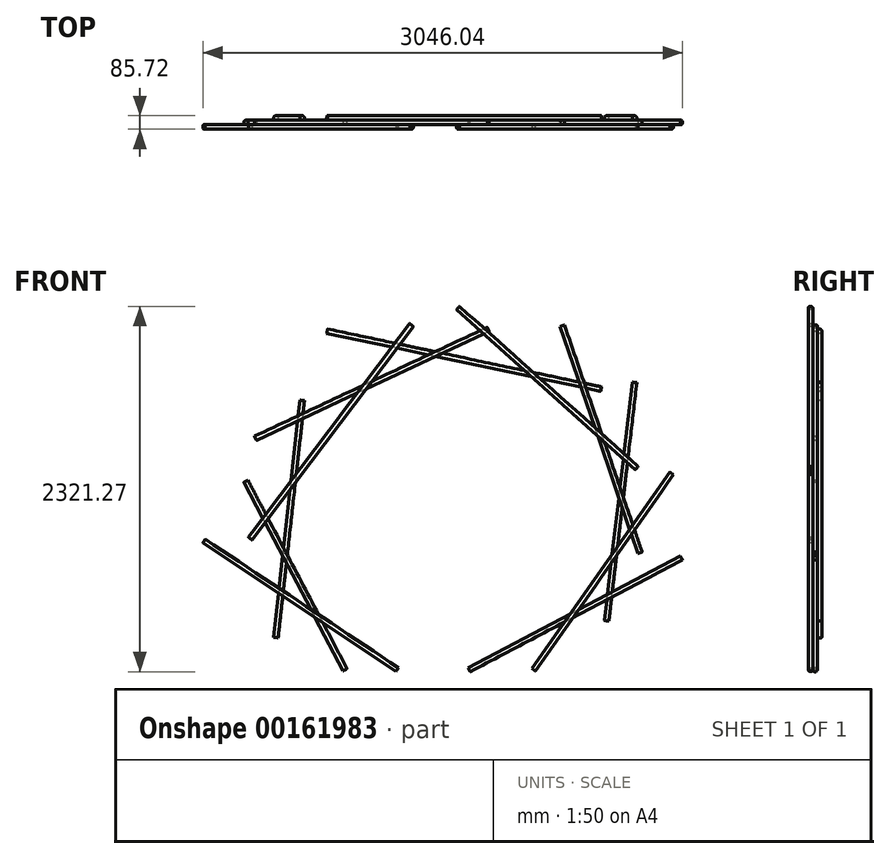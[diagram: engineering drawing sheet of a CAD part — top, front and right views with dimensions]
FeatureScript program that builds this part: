
annotation { "Feature Type Name" : "Feature", "Feature Type Description" : "" }
export const myFeature = defineFeature(function(context is Context, id is Id, definition is map)
    precondition{}
    {
        {
            var Q0;
            Q0=qCreatedBy(makeId("Front.planeOp"),FACE);
            var sketch = newSketch(context, id + "F0", { "sketchPlane" : qUnion([Q0])});
            skLineSegment(sketch, "E0", {"start": v(0, 0) * mm, "end": v(1347.88, 711.2) * mm});
            skSolve(sketch);
        }
        {
            var Q0;
            Q0=qCreatedBy(makeId("Front.planeOp"),FACE);
            var sketch = newSketch(context, id + "F1", { "sketchPlane" : qUnion([Q0])});
            skLineSegment(sketch, "E1", {"start": v(0, 0) * mm, "end": v(1289.35, 691.04) * mm});
            skLineSegment(sketch, "E2", {"start": v(401.37, 0) * mm, "end": v(1263.01, 1233.96) * mm});
            skLineSegment(sketch, "E3", {"start": v(865.33, 263.85) * mm, "end": v(1082.25, 1824.45) * mm});
            skLineSegment(sketch, "E4", {"start": v(1034.04, 757.94) * mm, "end": v(618.28, 2155.85) * mm});
            skLineSegment(sketch, "E5", {"start": v(1058.14, 1270.1) * mm, "end": v(-140.93, 2336.62) * mm});
            skLineSegment(sketch, "E6", {"start": v(811.1, 1803.36) * mm, "end": v(-900.14, 2149.83) * mm});
            skLineSegment(sketch, "E7", {"start": v(142.27, 2173.93) * mm, "end": v(-1358.07, 1474.97) * mm});
            skLineSegment(sketch, "E8", {"start": v(-363.87, 2192) * mm, "end": v(-1400.25, 830.25) * mm});
            skLineSegment(sketch, "E9", {"start": v(-1056.8, 1703.94) * mm, "end": v(-1225.51, 203.6) * mm});
            skLineSegment(sketch, "E10", {"start": v(-1418.33, 1197.8) * mm, "end": v(-787.5, 0) * mm});
            skLineSegment(sketch, "E11", {"start": v(-1683.45, 818.2) * mm, "end": v(-455.66, 0) * mm});
            skPoint(sketch, "E12", {"position": v(1003.15, 861.81) * mm});
            skPoint(sketch, "E13", {"position": v(965.87, 987.17) * mm});
            skPoint(sketch, "E14", {"position": v(818.26, 1483.47) * mm});
            skPoint(sketch, "E15", {"position": v(717.48, 1822.32) * mm});
            skPoint(sketch, "E16", {"position": v(76.46, 2143.27) * mm});
            skPoint(sketch, "E17", {"position": v(-209.58, 2010.01) * mm});
            skPoint(sketch, "E18", {"position": v(-663.2, 1798.69) * mm});
            skPoint(sketch, "E19", {"position": v(-1067.31, 1610.43) * mm});
            skPoint(sketch, "E20", {"position": v(-1296.53, 966.53) * mm});
            skPoint(sketch, "E21", {"position": v(-1167.3, 721.18) * mm});
            skPoint(sketch, "E22", {"position": v(-966.93, 340.71) * mm});
            skSolve(sketch);
        }
        {
            var Q0;
            Q0=sQuery(id+"F1.wireOp",EDGE,"E1");
            var Q1;
            Q1=sQuery(id+"F1.wireOp",VERTEX,"E1.start");
            cPlane(context, id + "F2", {"entities" : qUnion([Q0, Q1]), "cplaneType" : CPlaneType.LINE_POINT, "offset" : 25.4 * mm, "width" : 152.4 * mm, "height" : 152.4 * mm});
        }
        {
            var Q0;
            Q0=qCreatedBy(id+"F2.planeOp",FACE);
            var sketch = newSketch(context, id + "F3", { "sketchPlane" : qUnion([Q0])});
            skCircle(sketch, "E23", {"center": v(0, 0) * mm, "radius": 14.29 * mm});
            skSolve(sketch);
        }
        {
            var Q0;
            Q0 = qSketchRegion(id + "F3", true);
            var Q1;
            Q1=sQuery(id+"F0.wireOp",EDGE,"E0");
            sweep(context, id + "F4", {"profiles" : qUnion([Q0]), "path" : qUnion([Q1])});
        }
        {
            var Q0;
            Q0=qCreatedBy(makeId("Front.planeOp"),FACE);
            cPlane(context, id + "F5", {"entities" : qUnion([Q0]), "cplaneType" : CPlaneType.OFFSET, "offset" : 28.57 * mm, "oppositeDirection" : true, "width" : 152.4 * mm, "height" : 152.4 * mm});
        }
        {
            var Q0;
            Q0=qCreatedBy(makeId("Front.planeOp"),FACE);
            cPlane(context, id + "F6", {"entities" : qUnion([Q0]), "cplaneType" : CPlaneType.OFFSET, "offset" : 28.57 * mm, "width" : 152.4 * mm, "height" : 152.4 * mm});
        }
        {
            var Q0;
            Q0=qCreatedBy(id+"F6.planeOp",FACE);
            var sketch = newSketch(context, id + "F7", { "sketchPlane" : qUnion([Q0])});
            skLineSegment(sketch, "E24", {"start": v(410.8, 0) * mm, "end": v(1285.92, 1247.7) * mm});
            skSolve(sketch);
        }
        {
            var Q0;
            Q0=sQuery(id+"F7.wireOp",EDGE,"E24");
            var Q1;
            Q1=sQuery(id+"F7.wireOp",VERTEX,"E24.start");
            cPlane(context, id + "F8", {"entities" : qUnion([Q0, Q1]), "cplaneType" : CPlaneType.LINE_POINT, "offset" : 25.4 * mm, "width" : 152.4 * mm, "height" : 152.4 * mm});
        }
        {
            var Q0;
            Q0=qCreatedBy(id+"F8.planeOp",FACE);
            var sketch = newSketch(context, id + "F9", { "sketchPlane" : qUnion([Q0])});
            skCircle(sketch, "E25", {"center": v(336.32, -28.58) * mm, "radius": 14.29 * mm});
            skSolve(sketch);
        }
        {
            var Q0;
            Q0=makeQuery(id+"F9.imprint","IMPRINT",FACE,{"disambiguationData":[TD([[makeQuery(id+"F9.imprint","IMPRINT",EDGE,{"derivedFrom":sQuery(id+"F9.wireOp",EDGE,"E25")}),1.0]])]});
            var Q1;
            Q1=sQuery(id+"F7.wireOp",EDGE,"E24");
            sweep(context, id + "F10", {"profiles" : qUnion([Q0]), "path" : qUnion([Q1])});
        }
        {
            var Q0;
            Q0=qCreatedBy(id+"F5.planeOp",FACE);
            var sketch = newSketch(context, id + "F11", { "sketchPlane" : qUnion([Q0])});
            skLineSegment(sketch, "E26", {"start": v(873.47, 311.64) * mm, "end": v(1050.7, 1825.3) * mm});
            skSolve(sketch);
        }
        {
            var Q0;
            Q0=sQuery(id+"F11.wireOp",EDGE,"E26");
            var Q1;
            Q1=sQuery(id+"F11.wireOp",VERTEX,"E26.start");
            cPlane(context, id + "F12", {"entities" : qUnion([Q0, Q1]), "cplaneType" : CPlaneType.LINE_POINT, "offset" : 25.4 * mm, "width" : 152.4 * mm, "height" : 152.4 * mm});
        }
        {
            var Q0;
            Q0=qCreatedBy(id+"F12.planeOp",FACE);
            var sketch = newSketch(context, id + "F13", { "sketchPlane" : qUnion([Q0])});
            skCircle(sketch, "E27", {"center": v(831.3, 28.58) * mm, "radius": 14.29 * mm});
            skSolve(sketch);
        }
        {
            var Q0;
            Q0=makeQuery(id+"F13.imprint","IMPRINT",FACE,{"disambiguationData":[TD([[makeQuery(id+"F13.imprint","IMPRINT",EDGE,{"derivedFrom":sQuery(id+"F13.wireOp",EDGE,"E27")}),1.0]])]});
            var Q1;
            Q1=sQuery(id+"F13.wireOp",EDGE,"E27");
            var Q2;
            Q2=sQuery(id+"F11.wireOp",EDGE,"E26");
            sweep(context, id + "F14", {"profiles" : qUnion([Q0]), "surfaceProfiles" : qUnion([Q1]), "path" : qUnion([Q2])});
        }
        {
            var Q0;
            Q0=qCreatedBy(makeId("Front.planeOp"),FACE);
            var sketch = newSketch(context, id + "F15", { "sketchPlane" : qUnion([Q0])});
            skLineSegment(sketch, "E28", {"start": v(1085.24, 743.51) * mm, "end": v(591.85, 2185.44) * mm});
            skSolve(sketch);
        }
        {
            var Q0;
            Q0=sQuery(id+"F15.wireOp",EDGE,"E28");
            var Q1;
            Q1=sQuery(id+"F15.wireOp",VERTEX,"E28.start");
            cPlane(context, id + "F16", {"entities" : qUnion([Q0, Q1]), "cplaneType" : CPlaneType.LINE_POINT, "offset" : 25.4 * mm, "width" : 152.4 * mm, "height" : 152.4 * mm});
        }
        {
            var Q0;
            Q0=qCreatedBy(id+"F16.planeOp",FACE);
            var sketch = newSketch(context, id + "F17", { "sketchPlane" : qUnion([Q0])});
            skCircle(sketch, "E29", {"center": v(1267.5, 0) * mm, "radius": 14.29 * mm});
            skSolve(sketch);
        }
        {
            var Q0;
            Q0=makeQuery(id+"F17.imprint","IMPRINT",FACE,{"disambiguationData":[TD([[makeQuery(id+"F17.imprint","IMPRINT",EDGE,{"derivedFrom":sQuery(id+"F17.wireOp",EDGE,"E29")}),1.0]])]});
            var Q1;
            Q1 = qConstructionFilter(qBodyType(qCreatedBy(id + "F15" ,EDGE), BodyType.WIRE), ConstructionObject.NO);
            sweep(context, id + "F18", {"profiles" : qUnion([Q0]), "path" : qUnion([Q1])});
        }
        {
            var Q0;
            Q0=qCreatedBy(id+"F6.planeOp",FACE);
            var sketch = newSketch(context, id + "F19", { "sketchPlane" : qUnion([Q0])});
            skLineSegment(sketch, "E30", {"start": v(1064.5, 1281.28) * mm, "end": v(-70.75, 2298.04) * mm});
            skSolve(sketch);
        }
        {
            var Q0;
            Q0=sQuery(id+"F19.wireOp",EDGE,"E30");
            var Q1;
            Q1=sQuery(id+"F19.wireOp",VERTEX,"E30.start");
            cPlane(context, id + "F20", {"entities" : qUnion([Q0, Q1]), "cplaneType" : CPlaneType.LINE_POINT, "offset" : 25.4 * mm, "width" : 152.4 * mm, "height" : 152.4 * mm});
        }
        {
            var Q0;
            Q0=qCreatedBy(id+"F20.planeOp",FACE);
            var sketch = newSketch(context, id + "F21", { "sketchPlane" : qUnion([Q0])});
            skCircle(sketch, "E31", {"center": v(28.58, 1664.63) * mm, "radius": 14.29 * mm});
            skSolve(sketch);
        }
        {
            var Q0;
            Q0=makeQuery(id+"F21.imprint","IMPRINT",FACE,{"disambiguationData":[TD([[makeQuery(id+"F21.imprint","IMPRINT",EDGE,{"derivedFrom":sQuery(id+"F21.wireOp",EDGE,"E31")}),1.0]])]});
            var Q1;
            Q1 = qConstructionFilter(qBodyType(qCreatedBy(id + "F19" ,EDGE), BodyType.WIRE), ConstructionObject.NO);
            sweep(context, id + "F22", {"profiles" : qUnion([Q0]), "path" : qUnion([Q1])});
        }
        {
            var Q0;
            Q0=qCreatedBy(id+"F5.planeOp",FACE);
            var sketch = newSketch(context, id + "F23", { "sketchPlane" : qUnion([Q0])});
            skLineSegment(sketch, "E32", {"start": v(838.3, 1783.22) * mm, "end": v(-901.25, 2150.95) * mm});
            skSolve(sketch);
        }
        {
            var Q0;
            Q0=sQuery(id+"F23.wireOp",VERTEX,"E32.start");
            var Q1;
            Q1=sQuery(id+"F23.wireOp",EDGE,"E32");
            cPlane(context, id + "F24", {"entities" : qUnion([Q0, Q1]), "cplaneType" : CPlaneType.LINE_POINT, "offset" : 25.4 * mm, "width" : 152.4 * mm, "height" : 152.4 * mm});
        }
        {
            var Q0;
            Q0=qCreatedBy(id+"F24.planeOp",FACE);
            var sketch = newSketch(context, id + "F25", { "sketchPlane" : qUnion([Q0])});
            skCircle(sketch, "E33", {"center": v(-28.58, 1918.05) * mm, "radius": 14.29 * mm});
            skSolve(sketch);
        }
        {
            var Q0;
            Q0=makeQuery(id+"F25.imprint","IMPRINT",FACE,{"disambiguationData":[TD([[makeQuery(id+"F25.imprint","IMPRINT",EDGE,{"derivedFrom":sQuery(id+"F25.wireOp",EDGE,"E33")}),1.0]])]});
            var Q1;
            Q1=sQuery(id+"F23.wireOp",EDGE,"E32");
            sweep(context, id + "F26", {"profiles" : qUnion([Q0]), "path" : qUnion([Q1])});
        }
        {
            var Q0;
            Q0=qCreatedBy(makeId("Front.planeOp"),FACE);
            var sketch = newSketch(context, id + "F27", { "sketchPlane" : qUnion([Q0])});
            skLineSegment(sketch, "E34", {"start": v(121.58, 2162.72) * mm, "end": v(-1357.57, 1470.9) * mm});
            skSolve(sketch);
        }
        {
            var Q0;
            Q0=sQuery(id+"F27.wireOp",VERTEX,"E34.start");
            var Q1;
            Q1=sQuery(id+"F27.wireOp",EDGE,"E34");
            cPlane(context, id + "F28", {"entities" : qUnion([Q0, Q1]), "cplaneType" : CPlaneType.LINE_POINT, "offset" : 25.4 * mm, "width" : 152.4 * mm, "height" : 152.4 * mm});
        }
        {
            var Q0;
            Q0=qCreatedBy(id+"F28.planeOp",FACE);
            var sketch = newSketch(context, id + "F29", { "sketchPlane" : qUnion([Q0])});
            skCircle(sketch, "E35", {"center": v(0, 1907.53) * mm, "radius": 14.29 * mm});
            skSolve(sketch);
        }
        {
            var Q0;
            Q0=makeQuery(id+"F29.imprint","IMPRINT",FACE,{"disambiguationData":[TD([[makeQuery(id+"F29.imprint","IMPRINT",EDGE,{"derivedFrom":sQuery(id+"F29.wireOp",EDGE,"E35")}),1.0]])]});
            var Q1;
            Q1=sQuery(id+"F27.wireOp",EDGE,"E34");
            sweep(context, id + "F30", {"profiles" : qUnion([Q0]), "path" : qUnion([Q1])});
        }
        {
            var Q0;
            Q0=qCreatedBy(id+"F6.planeOp",FACE);
            var sketch = newSketch(context, id + "F31", { "sketchPlane" : qUnion([Q0])});
            skLineSegment(sketch, "E36", {"start": v(-365.8, 2190.11) * mm, "end": v(-1391.07, 833.98) * mm});
            skSolve(sketch);
        }
        {
            var Q0;
            Q0=sQuery(id+"F31.wireOp",EDGE,"E36");
            var Q1;
            Q1=sQuery(id+"F31.wireOp",VERTEX,"E36.start");
            cPlane(context, id + "F32", {"entities" : qUnion([Q0, Q1]), "cplaneType" : CPlaneType.LINE_POINT, "offset" : 25.4 * mm, "width" : 152.4 * mm, "height" : 152.4 * mm});
        }
        {
            var Q0;
            Q0=qCreatedBy(id+"F32.planeOp",FACE);
            var sketch = newSketch(context, id + "F33", { "sketchPlane" : qUnion([Q0])});
            skCircle(sketch, "E37", {"center": v(-1612.59, 28.58) * mm, "radius": 14.29 * mm});
            skSolve(sketch);
        }
        {
            var Q0;
            Q0=makeQuery(id+"F33.imprint","IMPRINT",FACE,{"disambiguationData":[TD([[makeQuery(id+"F33.imprint","IMPRINT",EDGE,{"derivedFrom":sQuery(id+"F33.wireOp",EDGE,"E37")}),1.0]])]});
            var Q1;
            Q1=sQuery(id+"F31.wireOp",EDGE,"E36");
            sweep(context, id + "F34", {"profiles" : qUnion([Q0]), "path" : qUnion([Q1])});
        }
        {
            var Q0;
            Q0=qCreatedBy(id+"F5.planeOp",FACE);
            var sketch = newSketch(context, id + "F35", { "sketchPlane" : qUnion([Q0])});
            skLineSegment(sketch, "E38", {"start": v(-1060.32, 1711.17) * mm, "end": v(-1227.3, 205.06) * mm});
            skSolve(sketch);
        }
        {
            var Q0;
            Q0=sQuery(id+"F35.wireOp",VERTEX,"E38.start");
            var Q1;
            Q1=sQuery(id+"F1.wireOp",EDGE,"E9");
            cPlane(context, id + "F36", {"entities" : qUnion([Q0, Q1]), "cplaneType" : CPlaneType.LINE_POINT, "offset" : 25.4 * mm, "width" : 152.4 * mm, "height" : 152.4 * mm});
        }
        {
            var Q0;
            Q0=qCreatedBy(id+"F36.planeOp",FACE);
            var sketch = newSketch(context, id + "F37", { "sketchPlane" : qUnion([Q0])});
            skCircle(sketch, "E39", {"center": v(-1244.9, -28.58) * mm, "radius": 14.29 * mm});
            skSolve(sketch);
        }
        {
            var Q0;
            Q0=makeQuery(id+"F37.imprint","IMPRINT",FACE,{"disambiguationData":[TD([[makeQuery(id+"F37.imprint","IMPRINT",EDGE,{"derivedFrom":sQuery(id+"F37.wireOp",EDGE,"E39")}),1.0]])]});
            var Q1;
            Q1=sQuery(id+"F35.wireOp",EDGE,"E38");
            sweep(context, id + "F38", {"profiles" : qUnion([Q0]), "path" : qUnion([Q1])});
        }
        {
            var Q0;
            Q0=qCreatedBy(makeId("Front.planeOp"),FACE);
            var sketch = newSketch(context, id + "F39", { "sketchPlane" : qUnion([Q0])});
            skLineSegment(sketch, "E40", {"start": v(-787.4, 0) * mm, "end": v(-1417.72, 1198) * mm});
            skSolve(sketch);
        }
        {
            var Q0;
            Q0=sQuery(id+"F39.wireOp",VERTEX,"E40.end");
            var Q1;
            Q1=sQuery(id+"F39.wireOp",EDGE,"E40");
            cPlane(context, id + "F40", {"entities" : qUnion([Q0, Q1]), "cplaneType" : CPlaneType.LINE_POINT, "offset" : 25.4 * mm, "width" : 152.4 * mm, "height" : 152.4 * mm});
        }
        {
            var Q0;
            Q0=qCreatedBy(id+"F40.planeOp",FACE);
            var sketch = newSketch(context, id + "F41", { "sketchPlane" : qUnion([Q0])});
            skCircle(sketch, "E41", {"center": v(-696.83, 0) * mm, "radius": 14.29 * mm});
            skSolve(sketch);
        }
        {
            var Q0;
            Q0=makeQuery(id+"F41.imprint","IMPRINT",FACE,{"disambiguationData":[TD([[makeQuery(id+"F41.imprint","IMPRINT",EDGE,{"derivedFrom":sQuery(id+"F41.wireOp",EDGE,"E41")}),1.0]])]});
            var Q1;
            Q1=sQuery(id+"F39.wireOp",EDGE,"E40");
            sweep(context, id + "F42", {"profiles" : qUnion([Q0]), "path" : qUnion([Q1])});
        }
        {
            var Q0;
            Q0=qCreatedBy(id+"F6.planeOp",FACE);
            var sketch = newSketch(context, id + "F43", { "sketchPlane" : qUnion([Q0])});
            skLineSegment(sketch, "E42", {"start": v(-455.13, 0) * mm, "end": v(-1682.05, 817.19) * mm});
            skSolve(sketch);
        }
        {
            var Q0;
            Q0=sQuery(id+"F1.wireOp",VERTEX,"E11.start");
            var Q1;
            Q1=sQuery(id+"F43.wireOp",EDGE,"E42");
            cPlane(context, id + "F44", {"entities" : qUnion([Q0, Q1]), "cplaneType" : CPlaneType.LINE_POINT, "offset" : 25.4 * mm, "width" : 152.4 * mm, "height" : 152.4 * mm});
        }
        {
            var Q0;
            Q0=qCreatedBy(id+"F44.planeOp",FACE);
            var sketch = newSketch(context, id + "F45", { "sketchPlane" : qUnion([Q0])});
            skCircle(sketch, "E43", {"center": v(28.58, -252.3) * mm, "radius": 14.29 * mm});
            skSolve(sketch);
        }
        {
            var Q0;
            Q0=makeQuery(id+"F45.imprint","IMPRINT",FACE,{"disambiguationData":[TD([[makeQuery(id+"F45.imprint","IMPRINT",EDGE,{"derivedFrom":sQuery(id+"F45.wireOp",EDGE,"E43")}),1.0]])]});
            var Q1;
            Q1=sQuery(id+"F43.wireOp",EDGE,"E42");
            sweep(context, id + "F46", {"profiles" : qUnion([Q0]), "path" : qUnion([Q1])});
        }
    });
